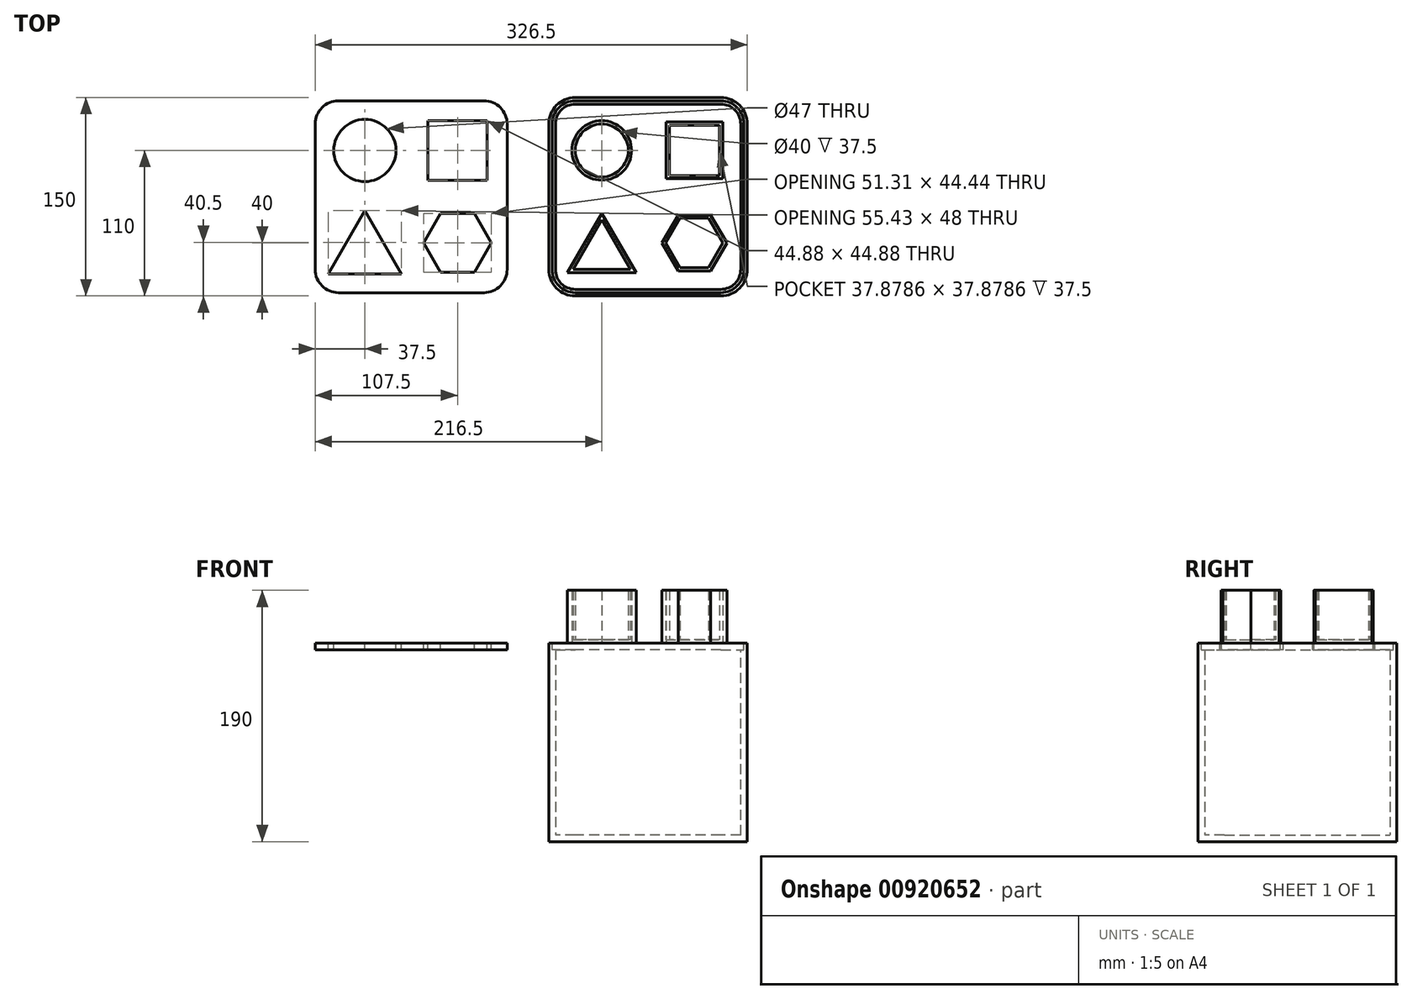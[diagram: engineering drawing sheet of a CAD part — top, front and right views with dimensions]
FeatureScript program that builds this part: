
annotation { "Feature Type Name" : "Feature", "Feature Type Description" : "" }
export const myFeature = defineFeature(function(context is Context, id is Id, definition is map)
    precondition{}
    {
        {
            var Q0;
            Q0=qCreatedBy(makeId("Top.planeOp"),FACE);
            var sketch = newSketch(context, id + "F0", { "sketchPlane" : qUnion([Q0])});
            skLineSegment(sketch, "E0.bottom", {"start": v(-20, 0) * mm, "end": v(-130, 0) * mm});
            skLineSegment(sketch, "E0.top", {"start": v(-20, 150) * mm, "end": v(-130, 150) * mm});
            skLineSegment(sketch, "E0.left", {"start": v(0, 20) * mm, "end": v(0, 130) * mm});
            skLineSegment(sketch, "E0.right", {"start": v(-150, 20) * mm, "end": v(-150, 130) * mm});
            skPoint(sketch, "E1.visualSharp", {"position": v(-150, 150) * mm});
            skArc(sketch, "E1.filletArc", {"start": v(-130, 150) * mm, "mid": v(-144.14, 144.14) * mm, "end": v(-150, 130) * mm});
            skPoint(sketch, "E2.visualSharp", {"position": v(0, 150) * mm});
            skArc(sketch, "E2.filletArc", {"start": v(0, 130) * mm, "mid": v(-5.86, 144.14) * mm, "end": v(-20, 150) * mm});
            skPoint(sketch, "E3.visualSharp", {"position": v(0, 0) * mm});
            skArc(sketch, "E3.filletArc", {"start": v(-20, 0) * mm, "mid": v(-5.86, 5.86) * mm, "end": v(0, 20) * mm});
            skPoint(sketch, "E4.visualSharp", {"position": v(-150, 0) * mm});
            skArc(sketch, "E4.filletArc", {"start": v(-150, 20) * mm, "mid": v(-144.14, 5.86) * mm, "end": v(-130, 0) * mm});
            skSolve(sketch);
        }
        {
            var Q0;
            Q0=makeQuery(id+"F0.imprint","IMPRINT",FACE,{"disambiguationData":[TD([[makeQuery(id+"F0.imprint","IMPRINT",EDGE,{"derivedFrom":sQuery(id+"F0.wireOp",EDGE,"E0.bottom")}),-1.0]])]});
            extrude(context, id + "F1", {"entities" : qUnion([Q0]), "depth" : 150 * mm, "offsetDistance" : 25 * mm});
        }
        {
            var Q0;
            Q0=makeQuery(id+"F1.opExtrude","CAP_FACE",FACE,{"disambiguationData":[OSD([sQuery(id+"F0.wireOp",EDGE,"E0.bottom"),sQuery(id+"F0.wireOp",EDGE,"E0.top"),sQuery(id+"F0.wireOp",EDGE,"E0.left"),sQuery(id+"F0.wireOp",EDGE,"E0.right")])],"isStart":false});
            var Q1;
            Q1=makeQuery(id+"F1.opExtrude","SWEPT_BODY",BODY,{"disambiguationData":[OSD([sQuery(id+"F0.wireOp",EDGE,"E0.bottom"),sQuery(id+"F0.wireOp",EDGE,"E0.top"),sQuery(id+"F0.wireOp",EDGE,"E0.left"),sQuery(id+"F0.wireOp",EDGE,"E0.right")])]});
            shell(context, id + "F2", {"entities" : qUnion([Q0]), "parts" : qUnion([Q1]), "thickness" : 5 * mm});
        }
        {
            var Q0;
            Q0=makeQuery(id+"F1.opExtrude","CAP_FACE",FACE,{"disambiguationData":[OSD([sQuery(id+"F0.wireOp",EDGE,"E0.bottom"),sQuery(id+"F0.wireOp",EDGE,"E0.top"),sQuery(id+"F0.wireOp",EDGE,"E0.left"),sQuery(id+"F0.wireOp",EDGE,"E0.right"),sQuery(id+"F0.wireOp",EDGE,"E1.filletArc"),sQuery(id+"F0.wireOp",EDGE,"E2.filletArc"),sQuery(id+"F0.wireOp",EDGE,"E3.filletArc"),sQuery(id+"F0.wireOp",EDGE,"E4.filletArc")])],"isStart":false});
            var sketch = newSketch(context, id + "F3", { "sketchPlane" : qUnion([Q0])});
            skArc(sketch, "E5.0.0", {"start": v(0, 130) * mm, "mid": v(-5.86, 144.14) * mm, "end": v(-20, 150) * mm});
            skLineSegment(sketch, "E5.0.1", {"start": v(-20, 150) * mm, "end": v(-130, 150) * mm});
            skArc(sketch, "E5.0.2", {"start": v(-130, 150) * mm, "mid": v(-144.14, 144.14) * mm, "end": v(-150, 130) * mm});
            skLineSegment(sketch, "E5.0.3", {"start": v(-150, 130) * mm, "end": v(-150, 20) * mm});
            skArc(sketch, "E5.0.4", {"start": v(-150, 20) * mm, "mid": v(-144.14, 5.86) * mm, "end": v(-130, 0) * mm});
            skLineSegment(sketch, "E5.0.5", {"start": v(-130, 0) * mm, "end": v(-20, 0) * mm});
            skArc(sketch, "E5.0.6", {"start": v(-20, 0) * mm, "mid": v(-5.86, 5.86) * mm, "end": v(0, 20) * mm});
            skLineSegment(sketch, "E5.0.7", {"start": v(0, 20) * mm, "end": v(0, 130) * mm});
            skArc(sketch, "E6.0.0", {"start": v(-5, 130) * mm, "mid": v(-9.4, 140.6) * mm, "end": v(-20, 145) * mm});
            skLineSegment(sketch, "E6.0.1", {"start": v(-20, 145) * mm, "end": v(-130, 145) * mm});
            skArc(sketch, "E6.0.2", {"start": v(-130, 145) * mm, "mid": v(-140.6, 140.6) * mm, "end": v(-145, 130) * mm});
            skLineSegment(sketch, "E6.0.3", {"start": v(-145, 130) * mm, "end": v(-145, 20) * mm});
            skArc(sketch, "E6.0.4", {"start": v(-145, 20) * mm, "mid": v(-140.6, 9.4) * mm, "end": v(-130, 5) * mm});
            skLineSegment(sketch, "E6.0.5", {"start": v(-130, 5) * mm, "end": v(-20, 5) * mm});
            skArc(sketch, "E6.0.6", {"start": v(-20, 5) * mm, "mid": v(-9.4, 9.4) * mm, "end": v(-5, 20) * mm});
            skLineSegment(sketch, "E6.0.7", {"start": v(-5, 20) * mm, "end": v(-5, 130) * mm});
            skArc(sketch, "E7.0", {"start": v(-130, 147.5) * mm, "mid": v(-142.37, 142.37) * mm, "end": v(-147.5, 130) * mm});
            skLineSegment(sketch, "E7.1", {"start": v(-20, 147.5) * mm, "end": v(-130, 147.5) * mm});
            skLineSegment(sketch, "E7.2", {"start": v(-147.5, 130) * mm, "end": v(-147.5, 20) * mm});
            skArc(sketch, "E7.3", {"start": v(-2.5, 130) * mm, "mid": v(-7.63, 142.37) * mm, "end": v(-20, 147.5) * mm});
            skArc(sketch, "E7.4", {"start": v(-147.5, 20) * mm, "mid": v(-142.37, 7.63) * mm, "end": v(-130, 2.5) * mm});
            skLineSegment(sketch, "E7.5", {"start": v(-130, 2.5) * mm, "end": v(-20, 2.5) * mm});
            skArc(sketch, "E7.6", {"start": v(-20, 2.5) * mm, "mid": v(-7.63, 7.63) * mm, "end": v(-2.5, 20) * mm});
            skLineSegment(sketch, "E7.7", {"start": v(-2.5, 20) * mm, "end": v(-2.5, 130) * mm});
            skSolve(sketch);
        }
        {
            var Q0;
            Q0=makeQuery(id+"F3.imprint","IMPRINT",FACE,{"disambiguationData":[TD([[makeQuery(id+"F3.imprint","IMPRINT",EDGE,{"derivedFrom":sQuery(id+"F3.wireOp",EDGE,"E6.0.0")}),-1.0]])]});
            extrude(context, id + "F4", {"entities" : qUnion([Q0]), "operationType" : NewBodyOperationType.REMOVE, "oppositeDirection" : true, "depth" : 5 * mm, "offsetDistance" : 25 * mm});
        }
        {
            var Q0;
            Q0=makeQuery(id+"F3.imprint","IMPRINT",FACE,{"disambiguationData":[TD([[makeQuery(id+"F3.imprint","IMPRINT",EDGE,{"derivedFrom":sQuery(id+"F3.wireOp",EDGE,"E6.0.0")}),-1.0]])]});
            var Q1;
            Q1=makeQuery(id+"F3.imprint","IMPRINT",FACE,{"disambiguationData":[TD([[makeQuery(id+"F3.imprint","IMPRINT",EDGE,{"derivedFrom":sQuery(id+"F3.wireOp",EDGE,"E6.0.0")}),1.0]])]});
            extrude(context, id + "F5", {"entities" : qUnion([Q0, Q1]), "depth" : 0 * mm, "offsetDistance" : 25 * mm, "hasSecondDirection" : true, "secondDirectionOppositeDirection" : true, "secondDirectionDepth" : 5 * mm});
        }
        {
            var Q0;
            Q0=makeQuery(id+"F5.opExtrude","CAP_FACE",FACE,{"disambiguationData":[OSD([sQuery(id+"F3.wireOp",EDGE,"E7.0"),sQuery(id+"F3.wireOp",EDGE,"E7.1"),sQuery(id+"F3.wireOp",EDGE,"E7.2"),sQuery(id+"F3.wireOp",EDGE,"E7.3"),sQuery(id+"F3.wireOp",EDGE,"E7.4"),sQuery(id+"F3.wireOp",EDGE,"E7.5"),sQuery(id+"F3.wireOp",EDGE,"E7.6"),sQuery(id+"F3.wireOp",EDGE,"E7.7")])],"isStart":false});
            var sketch = newSketch(context, id + "F6", { "sketchPlane" : qUnion([Q0])});
            skLineSegment(sketch, "E8", {"start": v(-130, 130) * mm, "end": v(-20, 20) * mm, "construction": true});
            skCircle(sketch, "E9", {"center": v(-110, 110) * mm, "radius": 22.5 * mm});
            skCircle(sketch, "E10", {"center": v(-40, 110) * mm, "radius": 22.5 * mm, "construction": true});
            skLineSegment(sketch, "E11.bottom", {"start": v(-18.56, 131.44) * mm, "end": v(-61.44, 131.44) * mm});
            skLineSegment(sketch, "E11.top", {"start": v(-18.56, 88.56) * mm, "end": v(-61.44, 88.56) * mm});
            skLineSegment(sketch, "E11.left", {"start": v(-18.56, 131.44) * mm, "end": v(-18.56, 88.56) * mm});
            skLineSegment(sketch, "E11.right", {"start": v(-61.44, 131.44) * mm, "end": v(-61.44, 88.56) * mm});
            skLineSegment(sketch, "E12", {"start": v(-20, 130) * mm, "end": v(-130, 20) * mm, "construction": true});
            skLineSegment(sketch, "E13", {"start": v(-110, 110) * mm, "end": v(-110, 40) * mm, "construction": true});
            skLineSegment(sketch, "E14", {"start": v(-110, 40) * mm, "end": v(-40, 40) * mm, "construction": true});
            skCircle(sketch, "E15", {"center": v(-110, 40) * mm, "radius": 22.5 * mm, "construction": true});
            skLineSegment(sketch, "E16", {"start": v(-110, 110) * mm, "end": v(-40, 110) * mm, "construction": true});
            skLineSegment(sketch, "E17", {"start": v(-110, 62.5) * mm, "end": v(-135.98, 17.5) * mm});
            skLineSegment(sketch, "E18", {"start": v(-135.98, 17.5) * mm, "end": v(-84.02, 17.5) * mm});
            skLineSegment(sketch, "E19", {"start": v(-84.02, 17.5) * mm, "end": v(-110, 62.5) * mm});
            skCircle(sketch, "E20", {"center": v(-40, 40) * mm, "radius": 22.5 * mm, "construction": true});
            skCircle(sketch, "E21.cCircle", {"center": v(-40, 40) * mm, "radius": 24.5 * mm, "construction": true});
            skLineSegment(sketch, "E21.0", {"start": v(-27.75, 61.22) * mm, "end": v(-15.5, 40) * mm});
            skLineSegment(sketch, "E21.1", {"start": v(-15.5, 40) * mm, "end": v(-27.75, 18.78) * mm});
            skLineSegment(sketch, "E21.2", {"start": v(-27.75, 18.78) * mm, "end": v(-52.25, 18.78) * mm});
            skLineSegment(sketch, "E21.3", {"start": v(-52.25, 18.78) * mm, "end": v(-64.5, 40) * mm});
            skLineSegment(sketch, "E21.4", {"start": v(-64.5, 40) * mm, "end": v(-52.25, 61.22) * mm});
            skLineSegment(sketch, "E21.5", {"start": v(-52.25, 61.22) * mm, "end": v(-27.75, 61.22) * mm});
            skCircle(sketch, "E22.0", {"center": v(-110, 110) * mm, "radius": 23.5 * mm});
            skLineSegment(sketch, "E23.0", {"start": v(-17.56, 132.44) * mm, "end": v(-62.44, 132.44) * mm});
            skLineSegment(sketch, "E23.1", {"start": v(-17.56, 132.44) * mm, "end": v(-17.56, 87.56) * mm});
            skLineSegment(sketch, "E23.2", {"start": v(-17.56, 87.56) * mm, "end": v(-62.44, 87.56) * mm});
            skLineSegment(sketch, "E23.3", {"start": v(-62.44, 132.44) * mm, "end": v(-62.44, 87.56) * mm});
            skLineSegment(sketch, "E24.0", {"start": v(-82.29, 16.5) * mm, "end": v(-110, 64.5) * mm});
            skLineSegment(sketch, "E24.1", {"start": v(-137.71, 16.5) * mm, "end": v(-82.29, 16.5) * mm});
            skLineSegment(sketch, "E24.2", {"start": v(-110, 64.5) * mm, "end": v(-137.71, 16.5) * mm});
            skLineSegment(sketch, "E25.0", {"start": v(-52.83, 17.78) * mm, "end": v(-65.65, 40) * mm});
            skLineSegment(sketch, "E25.1", {"start": v(-52.83, 62.22) * mm, "end": v(-27.17, 62.22) * mm});
            skLineSegment(sketch, "E25.2", {"start": v(-27.17, 62.22) * mm, "end": v(-14.35, 40) * mm});
            skLineSegment(sketch, "E25.3", {"start": v(-65.65, 40) * mm, "end": v(-52.83, 62.22) * mm});
            skLineSegment(sketch, "E25.4", {"start": v(-14.35, 40) * mm, "end": v(-27.17, 17.78) * mm});
            skLineSegment(sketch, "E25.5", {"start": v(-27.17, 17.78) * mm, "end": v(-52.83, 17.78) * mm});
            skLineSegment(sketch, "E26.0", {"start": v(-130, -2.5) * mm, "end": v(-20, -2.5) * mm});
            skArc(sketch, "E26.1", {"start": v(-152.5, 20) * mm, "mid": v(-145.9, 4.1) * mm, "end": v(-130, -2.5) * mm});
            skArc(sketch, "E26.2", {"start": v(-20, -2.5) * mm, "mid": v(-4.1, 4.1) * mm, "end": v(2.5, 20) * mm});
            skLineSegment(sketch, "E26.3", {"start": v(-152.5, 130) * mm, "end": v(-152.5, 20) * mm});
            skLineSegment(sketch, "E26.4", {"start": v(2.5, 20) * mm, "end": v(2.5, 130) * mm});
            skArc(sketch, "E26.5", {"start": v(2.5, 130) * mm, "mid": v(-4.1, 145.9) * mm, "end": v(-20, 152.5) * mm});
            skLineSegment(sketch, "E26.6", {"start": v(-20, 152.5) * mm, "end": v(-130, 152.5) * mm});
            skArc(sketch, "E26.7", {"start": v(-130, 152.5) * mm, "mid": v(-145.9, 145.9) * mm, "end": v(-152.5, 130) * mm});
            skSolve(sketch);
        }
        {
            var Q0;
            Q0=makeQuery(id+"F6.imprint","IMPRINT",FACE,{"disambiguationData":[TD([[makeQuery(id+"F6.imprint","IMPRINT",EDGE,{"derivedFrom":sQuery(id+"F6.wireOp",EDGE,"E9")}),-1.0]])]});
            var Q1;
            Q1=makeQuery(id+"F6.imprint","IMPRINT",FACE,{"disambiguationData":[TD([[makeQuery(id+"F6.imprint","IMPRINT",EDGE,{"derivedFrom":sQuery(id+"F6.wireOp",EDGE,"E9")}),1.0]])]});
            var Q2;
            Q2=makeQuery(id+"F6.imprint","IMPRINT",FACE,{"disambiguationData":[TD([[makeQuery(id+"F6.imprint","IMPRINT",EDGE,{"derivedFrom":sQuery(id+"F6.wireOp",EDGE,"E11.bottom")}),-1.0]])]});
            var Q3;
            Q3=makeQuery(id+"F6.imprint","IMPRINT",FACE,{"disambiguationData":[TD([[makeQuery(id+"F6.imprint","IMPRINT",EDGE,{"derivedFrom":sQuery(id+"F6.wireOp",EDGE,"E11.bottom")}),1.0]])]});
            var Q4;
            Q4=makeQuery(id+"F6.imprint","IMPRINT",FACE,{"disambiguationData":[TD([[makeQuery(id+"F6.imprint","IMPRINT",EDGE,{"derivedFrom":sQuery(id+"F6.wireOp",EDGE,"E17")}),-1.0]])]});
            var Q5;
            Q5=makeQuery(id+"F6.imprint","IMPRINT",FACE,{"disambiguationData":[TD([[makeQuery(id+"F6.imprint","IMPRINT",EDGE,{"derivedFrom":sQuery(id+"F6.wireOp",EDGE,"E17")}),1.0]])]});
            var Q6;
            Q6=makeQuery(id+"F6.imprint","IMPRINT",FACE,{"disambiguationData":[TD([[makeQuery(id+"F6.imprint","IMPRINT",EDGE,{"derivedFrom":sQuery(id+"F6.wireOp",EDGE,"E21.0")}),-1.0]])]});
            var Q7;
            Q7=makeQuery(id+"F6.imprint","IMPRINT",FACE,{"disambiguationData":[TD([[makeQuery(id+"F6.imprint","IMPRINT",EDGE,{"derivedFrom":sQuery(id+"F6.wireOp",EDGE,"E21.0")}),1.0]])]});
            extrude(context, id + "F7", {"entities" : qUnion([Q0, Q1, Q2, Q3, Q4, Q5, Q6, Q7]), "operationType" : NewBodyOperationType.REMOVE, "endBound" : BoundingType.SYMMETRIC, "oppositeDirection" : true, "depth" : 25 * mm, "offsetDistance" : 25 * mm});
        }
        {
            var Q0;
            Q0=makeQuery(id+"F6.imprint","IMPRINT",FACE,{"disambiguationData":[TD([[makeQuery(id+"F6.imprint","IMPRINT",EDGE,{"derivedFrom":sQuery(id+"F6.wireOp",EDGE,"E9")}),1.0]])]});
            var Q1;
            Q1=makeQuery(id+"F6.imprint","IMPRINT",FACE,{"disambiguationData":[TD([[makeQuery(id+"F6.imprint","IMPRINT",EDGE,{"derivedFrom":sQuery(id+"F6.wireOp",EDGE,"E11.bottom")}),1.0]])]});
            var Q2;
            Q2=makeQuery(id+"F6.imprint","IMPRINT",FACE,{"disambiguationData":[TD([[makeQuery(id+"F6.imprint","IMPRINT",EDGE,{"derivedFrom":sQuery(id+"F6.wireOp",EDGE,"E17")}),1.0]])]});
            var Q3;
            Q3=makeQuery(id+"F6.imprint","IMPRINT",FACE,{"disambiguationData":[TD([[makeQuery(id+"F6.imprint","IMPRINT",EDGE,{"derivedFrom":sQuery(id+"F6.wireOp",EDGE,"E21.0")}),-1.0]])]});
            extrude(context, id + "F8", {"entities" : qUnion([Q0, Q1, Q2, Q3]), "depth" : 40 * mm, "offsetDistance" : 25 * mm});
        }
        {
            var Q0;
            Q0=makeQuery(id+"F8.opExtrude","CAP_FACE",FACE,{"disambiguationData":[OSD([sQuery(id+"F6.wireOp",EDGE,"E9")])],"isStart":false});
            var Q1;
            Q1=makeQuery(id+"F8.opExtrude","CAP_FACE",FACE,{"disambiguationData":[OSD([sQuery(id+"F6.wireOp",EDGE,"E11.bottom"),sQuery(id+"F6.wireOp",EDGE,"E11.top"),sQuery(id+"F6.wireOp",EDGE,"E11.left"),sQuery(id+"F6.wireOp",EDGE,"E11.right")])],"isStart":false});
            var Q2;
            Q2=makeQuery(id+"F8.opExtrude","CAP_FACE",FACE,{"disambiguationData":[OSD([sQuery(id+"F6.wireOp",EDGE,"E17"),sQuery(id+"F6.wireOp",EDGE,"E18"),sQuery(id+"F6.wireOp",EDGE,"E19")])],"isStart":false});
            var Q3;
            Q3=makeQuery(id+"F8.opExtrude","CAP_FACE",FACE,{"disambiguationData":[OSD([sQuery(id+"F6.wireOp",EDGE,"E21.0"),sQuery(id+"F6.wireOp",EDGE,"E21.1"),sQuery(id+"F6.wireOp",EDGE,"E21.2"),sQuery(id+"F6.wireOp",EDGE,"E21.3"),sQuery(id+"F6.wireOp",EDGE,"E21.4"),sQuery(id+"F6.wireOp",EDGE,"E21.5")])],"isStart":false});
            shell(context, id + "F9", {"entities" : qUnion([Q0, Q1, Q2, Q3]), "thickness" : 2.5 * mm});
        }
        {
            var Q0;
            Q0=makeQuery(id+"F5.opExtrude","SWEPT_BODY",BODY,{"disambiguationData":[OSD([sQuery(id+"F3.wireOp",EDGE,"E7.0"),sQuery(id+"F3.wireOp",EDGE,"E7.1"),sQuery(id+"F3.wireOp",EDGE,"E7.2"),sQuery(id+"F3.wireOp",EDGE,"E7.3"),sQuery(id+"F3.wireOp",EDGE,"E7.4"),sQuery(id+"F3.wireOp",EDGE,"E7.5"),sQuery(id+"F3.wireOp",EDGE,"E7.6"),sQuery(id+"F3.wireOp",EDGE,"E7.7")])]});
            transform(context, id + "F10", {"entities" : qUnion([Q0]), "transformType" : TransformType.TRANSLATION_3D, "dx" : -179 * mm, "dy" : 0 * mm, "dz" : 0 * mm, "makeCopy" : false});
        }
    });
